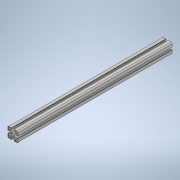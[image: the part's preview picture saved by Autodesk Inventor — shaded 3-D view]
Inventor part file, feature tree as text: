
AUTODESK INVENTOR PART (.ipt)
format: ipt  version: 2020 (Build 240168000, 168)  size: 221,696 bytes
history: native  units: mm
features: extrude x1, sketch x1
ambient origin geometry x8: Origin, YZ Plane, XZ Plane, XY Plane, X Axis, Y Axis, Z Axis, Center Point
bodies: Solid1 (feature_tree)
feature tree (2):
  extrude  "Extrusion1"  [1 undecoded]
  sketch  "Sketch1"  dims[d1=40.0mm d2=0.75mm d3=7.45mm d4=2.25mm d5=1.0mm d6=2.1mm d7=0.75mm d8=0.65mm d9=1.25mm d10=2.25mm d11=360.0deg d12=4.0mm d13=20.0mm d14=300.0mm d15=0.0mm]
note: 1 required parameter value undecoded (feature->parameter linkage not recoverable at this tier; creation-order binding heuristic only, values carry confidence <= 0.55)
